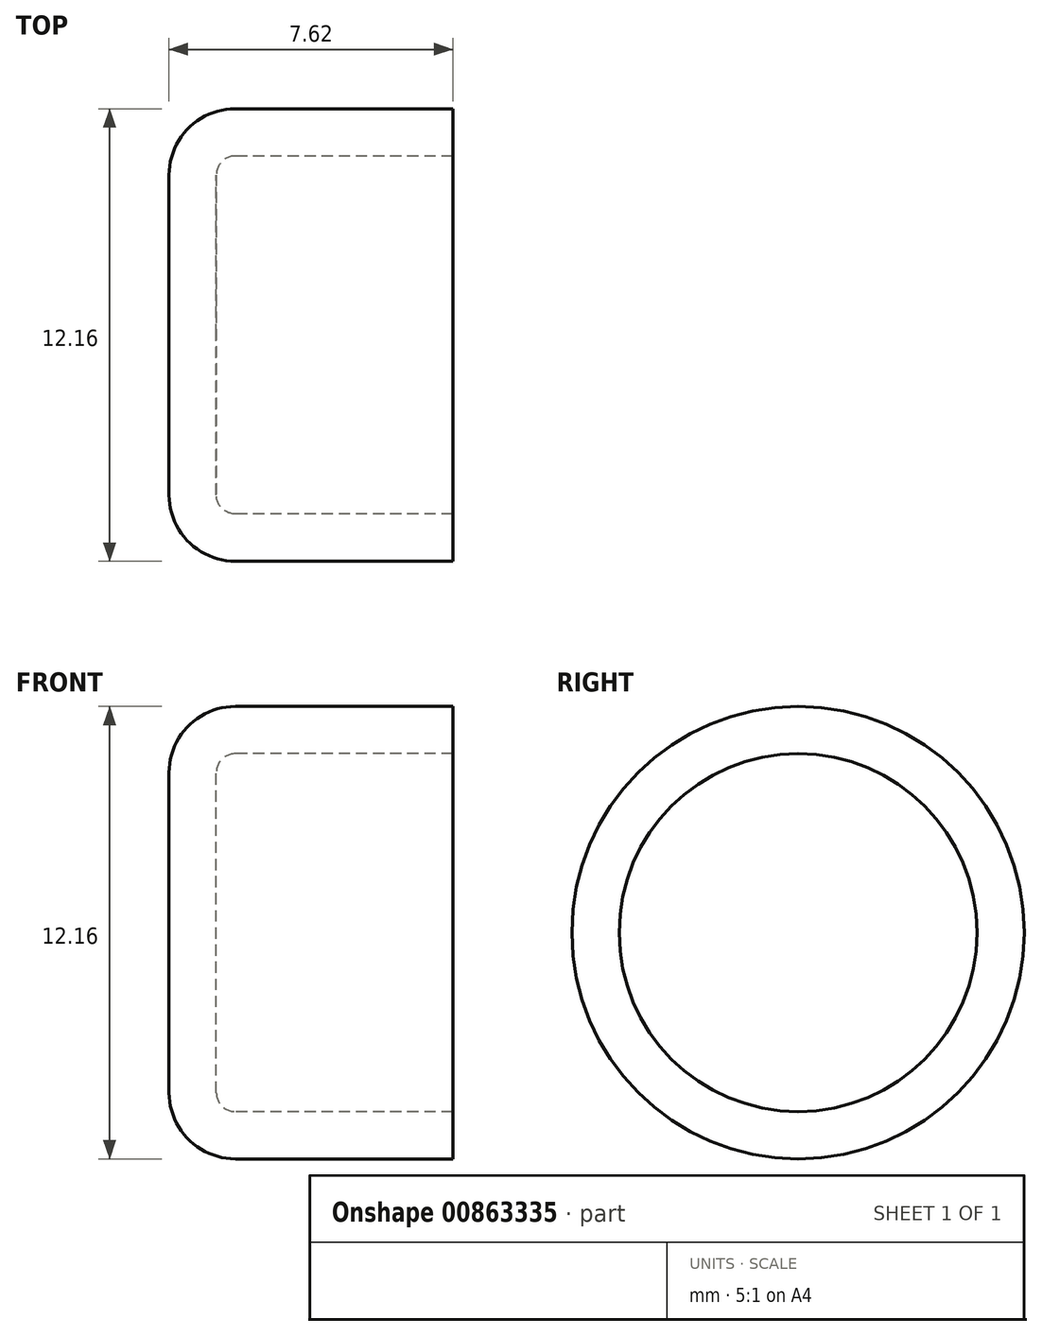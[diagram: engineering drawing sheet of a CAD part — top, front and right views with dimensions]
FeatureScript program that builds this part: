
annotation { "Feature Type Name" : "Feature", "Feature Type Description" : "" }
export const myFeature = defineFeature(function(context is Context, id is Id, definition is map)
    precondition{}
    {
        {
            var Q0;
            Q0=qCreatedBy(makeId("Right.planeOp"),FACE);
            var sketch = newSketch(context, id + "F0", { "sketchPlane" : qUnion([Q0])});
            skCircle(sketch, "E0", {"center": v(0, 0) * mm, "radius": 6.08 * mm});
            skSolve(sketch);
        }
        {
            var Q0;
            Q0=makeQuery(id+"F0.imprint","IMPRINT",FACE,{"disambiguationData":[TD([[makeQuery(id+"F0.imprint","IMPRINT",EDGE,{"derivedFrom":sQuery(id+"F0.wireOp",EDGE,"E0")}),1.0]])]});
            extrude(context, id + "F1", {"entities" : qUnion([Q0]), "depth" : 7.62 * mm, "offsetDistance" : 25.4 * mm});
        }
        {
            var Q0;
            Q0=makeQuery(id+"F1.opExtrude","CAP_EDGE",EDGE,{"disambiguationData":[OSD([sQuery(id+"F0.wireOp",EDGE,"E0")])],"isStart":true});
            fillet(context, id + "F2", {"entities" : qUnion([Q0]), "radius" : 1.78 * mm, "tangentPropagation" : true, "allowEdgeOverflow" : false});
        }
        {
            var Q0;
            Q0=makeQuery(id+"F1.opExtrude","CAP_FACE",FACE,{"disambiguationData":[OSD([sQuery(id+"F0.wireOp",EDGE,"E0")])],"isStart":false});
            shell(context, id + "F3", {"entities" : qUnion([Q0]), "thickness" : 1.27 * mm});
        }
    });
